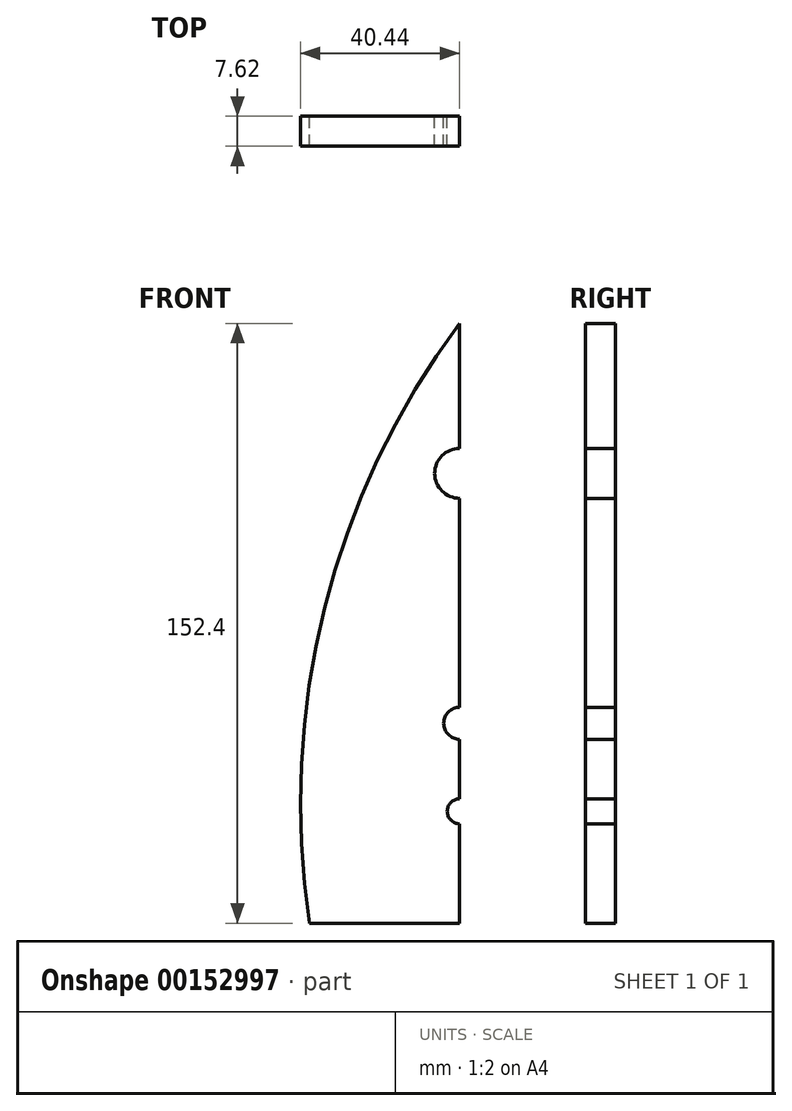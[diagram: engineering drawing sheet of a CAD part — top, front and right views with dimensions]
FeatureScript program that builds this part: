
annotation { "Feature Type Name" : "Feature", "Feature Type Description" : "" }
export const myFeature = defineFeature(function(context is Context, id is Id, definition is map)
    precondition{}
    {
        {
            var Q0;
            Q0=qCreatedBy(makeId("Front.planeOp"),FACE);
            var sketch = newSketch(context, id + "F0", { "sketchPlane" : qUnion([Q0])});
            skLineSegment(sketch, "E0", {"start": v(0, 101.6) * mm, "end": v(0, -50.8) * mm});
            skLineSegment(sketch, "E1", {"start": v(-38.1, -50.8) * mm, "end": v(38.1, -50.8) * mm});
            skArc(sketch, "E2", {"start": v(0, 101.6) * mm, "mid": v(-34.37, 29.23) * mm, "end": v(-38.1, -50.8) * mm});
            skArc(sketch, "E3.MirrorCS", {"start": v(0, 101.6) * mm, "mid": v(34.37, 29.23) * mm, "end": v(38.1, -50.8) * mm});
            skCircle(sketch, "E4", {"center": v(0, 63.5) * mm, "radius": 6.35 * mm});
            skCircle(sketch, "E5", {"center": v(0, 0) * mm, "radius": 4.06 * mm});
            skLineSegment(sketch, "E6", {"start": v(0, 0) * mm, "end": v(0, -22.35) * mm, "construction": true});
            skCircle(sketch, "E7", {"center": v(0, -22.35) * mm, "radius": 3.18 * mm});
            skSolve(sketch);
        }
        {
            var Q0;
            {var subQ0=sQuery(id+"F0.wireOp",EDGE,"E2");Q0=makeQuery(id+"F0.imprint","IMPRINT",FACE,{"disambiguationData":[TD([[makeQuery(id+"F0.imprint","IMPRINT",EDGE,{"derivedFrom":subQ0}),1.0]])]});}
            var Q1;
            {var subQ0=sQuery(id+"F0.wireOp",EDGE,"E3.MirrorCS");Q1=makeQuery(id+"F0.imprint","IMPRINT",FACE,{"disambiguationData":[TD([[makeQuery(id+"F0.imprint","IMPRINT",EDGE,{"derivedFrom":subQ0}),-1.0]])]});}
            extrude(context, id + "F1", {"entities" : qUnion([Q0, Q1]), "depth" : 7.62 * mm});
        }
    });
